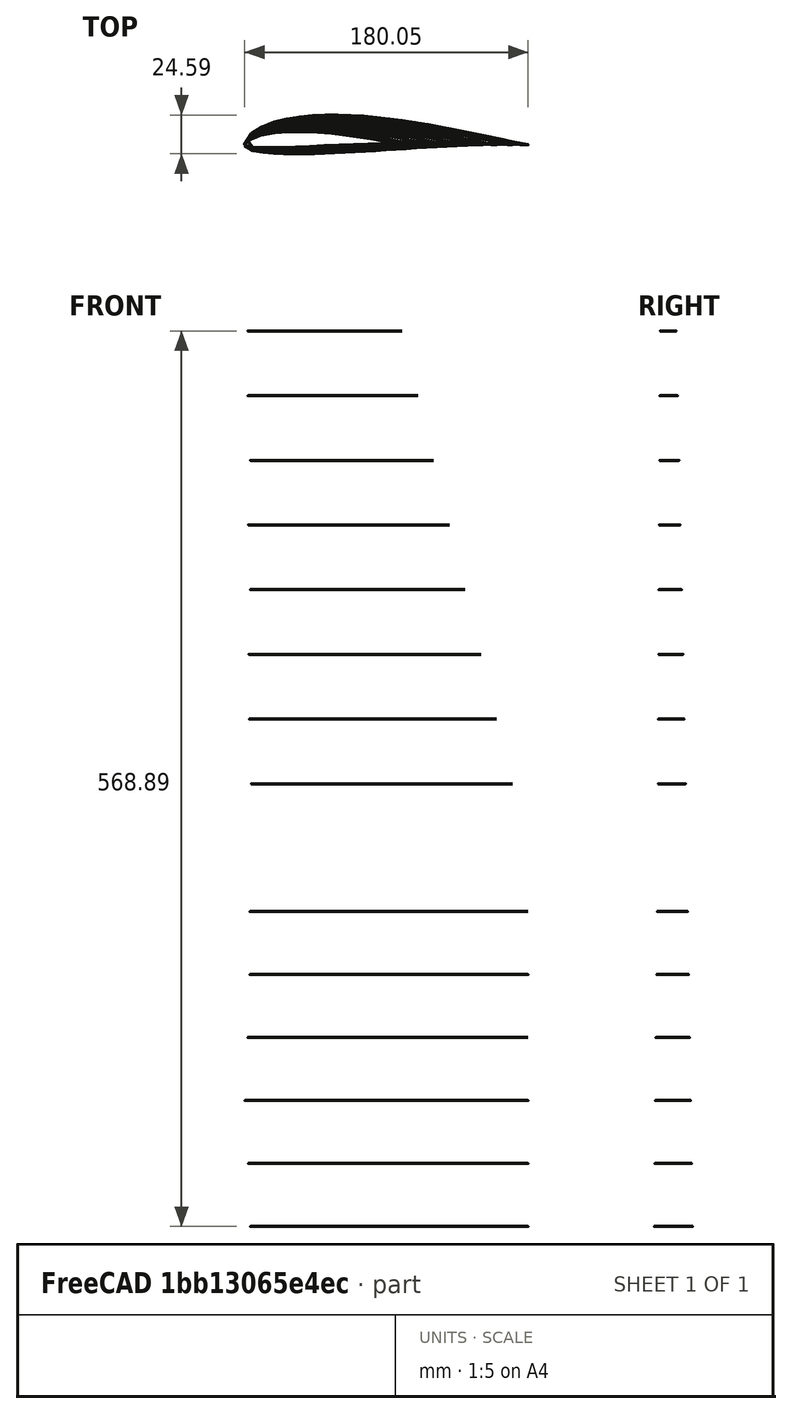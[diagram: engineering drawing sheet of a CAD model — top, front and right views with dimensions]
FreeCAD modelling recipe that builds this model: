
FCSTD DOCUMENT  (FreeCAD 0.21R33771 (Git))
Label: SD7034_wng9
License: All rights reserved
LicenseURL: http://en.wikipedia.org/wiki/All_rights_reserved
objects: Part::Part2DObjectPython×23, Part::MultiCommon×14, App::MeasureDistance×6, App::DocumentObjectGroup×2, Part::Loft×2
note: 39 computed .brp shape members not serialized (recipe doc carries the construction recipe); baked Part::Feature solids carry a one-line shape summary decoded from their .brp

FEATURE [App::DocumentObjectGroup] profile_sd7062_il  label="profile_sd7062-il"
FEATURE [Part::Part2DObjectPython] Wire  # Draft 2D object (typed FeaturePython)
  ChamferSize = 0
  Closed = true
  End = (1,0,0)
  FilletRadius = 0
  Length = 2.05949
  MakeFace = true
  Points = (61) [(1,0,0),(0.99652,0.00057,0),(0.98634,0.00242,0),(0.97004,0.00571,0),(0.94818,0.01036,0),(0.92127,0.01615,0),(0.88967,0.02289,0),(0.85381,0.03049,0),+53 more]
  Start = (1,0,0)
  Subdivisions = 0
FEATURE [Part::Part2DObjectPython] BSpline  # Draft 2D object (typed FeaturePython)
  Closed = true
  MakeFace = true
  Parameterization = 1
  Points = (60) [(1,0,0),(0.99652,0.00057,0),(0.98634,0.00242,0),(0.97004,0.00571,0),(0.94818,0.01036,0),(0.92127,0.01615,0),(0.88967,0.02289,0),(0.85381,0.03049,0),+52 more]
FEATURE [App::DocumentObjectGroup] profile_SD7032_099_88  label="profile_SD7032-099-88"
FEATURE [Part::Part2DObjectPython] Wire001  # Draft 2D object (typed FeaturePython)
  ChamferSize = 0
  Closed = true
  End = (1,0,0)
  FilletRadius = 0
  Length = 2.03505
  MakeFace = true
  Points = (61) [(1,0,0),(0.99674,0.00048,0),(0.98712,0.00204,0),(0.97155,0.00485,0),(0.95054,0.00894,0),(0.92464,0.0142,0),(0.89436,0.02041,0),(0.86021,0.02731,0),+53 more]
  Start = (1,0,0)
  Subdivisions = 0
FEATURE [Part::Part2DObjectPython] BSpline001  # Draft 2D object (typed FeaturePython)
  Closed = true
  MakeFace = true
  Parameterization = 1
  Points = (60) [(1,0,0),(0.99674,0.00048,0),(0.98712,0.00204,0),(0.97155,0.00485,0),(0.95054,0.00894,0),(0.92464,0.0142,0),(0.89436,0.02041,0),(0.86021,0.02731,0),+52 more]
FEATURE [Part::Part2DObjectPython] Clone2D  label="BSpline (2D)"  # Draft 2D object (typed FeaturePython)
  Fuse = false
  Objects = -> [BSpline]
  Scale = (180,180,1)
FEATURE [Part::Part2DObjectPython] Clone2D001  label="BSpline001 (2D)"  # Draft 2D object (typed FeaturePython)
  Fuse = false
  Objects = -> [BSpline001]
  Placement = pos=(0,0,280) rot=(0,0,1;0rad)
  Scale = (180,180,1)
FEATURE [Part::Loft] Loft
  Closed = false
  MaxDegree = 5
  Ruled = false
  Sections = -> [Clone2D,Clone2D001]
  Solid = true
FEATURE [Part::Part2DObjectPython] Clone2D002  label="BSpline001 (2D)001"  # Draft 2D object (typed FeaturePython)
  Fuse = false
  Objects = -> [BSpline001]
  Placement = pos=(0,0,280) rot=(0,0,1;0rad)
  Scale = (180,180,1)
FEATURE [Part::Part2DObjectPython] Clone2D003  label="BSpline001 (2D)002"  # Draft 2D object (typed FeaturePython)
  Fuse = false
  Objects = -> [BSpline001]
  Placement = pos=(0,0,650) rot=(0,0,1;0rad)
  Scale = (90,90,1)
FEATURE [Part::Loft] Loft001
  Closed = false
  MaxDegree = 5
  Ruled = false
  Sections = -> [Clone2D002,Clone2D003]
  Solid = true
FEATURE [Part::Part2DObjectPython] Rectangle  # Draft 2D object (typed FeaturePython)
  ChamferSize = 0
  Columns = 1
  FilletRadius = 0
  Height = 60
  Length = 220
  MakeFace = true
  Placement = pos=(-10,-15,0) rot=(0,0,1;0rad)
  Rows = 1
FEATURE [Part::Part2DObjectPython] Clone2D004  label="Rectangle (2D)"  # Draft 2D object (typed FeaturePython)
  Fuse = false
  Objects = -> [Rectangle]
  Placement = pos=(-15,-20,40) rot=(0,0,1;0rad)
  Scale = (1,1,1)
FEATURE [Part::MultiCommon] Common
  Shapes = -> [Clone2D004,Loft]
FEATURE [Part::Part2DObjectPython] Clone2D005  label="Rectangle (2D)001"  # Draft 2D object (typed FeaturePython)
  Fuse = false
  Objects = -> [Rectangle]
  Placement = pos=(-15,-20,80) rot=(0,0,1;0rad)
  Scale = (1,1,1)
FEATURE [Part::MultiCommon] Common001
  Shapes = -> [Clone2D005,Loft]
FEATURE [Part::Part2DObjectPython] Clone2D006  label="Rectangle (2D)002"  # Draft 2D object (typed FeaturePython)
  Fuse = false
  Objects = -> [Rectangle]
  Placement = pos=(-15,-20,120) rot=(0,0,1;0rad)
  Scale = (1,1,1)
FEATURE [Part::MultiCommon] Common002
  Shapes = -> [Clone2D006,Loft]
FEATURE [Part::Part2DObjectPython] Clone2D007  label="Rectangle (2D)003"  # Draft 2D object (typed FeaturePython)
  Fuse = false
  Objects = -> [Rectangle]
  Placement = pos=(-15,-20,160) rot=(0,0,1;0rad)
  Scale = (1,1,1)
FEATURE [Part::MultiCommon] Common003
  Shapes = -> [Clone2D007,Loft]
FEATURE [Part::Part2DObjectPython] Clone2D008  label="Rectangle (2D)004"  # Draft 2D object (typed FeaturePython)
  Fuse = false
  Objects = -> [Rectangle]
  Placement = pos=(-15,-20,200) rot=(0,0,1;0rad)
  Scale = (1,1,1)
FEATURE [Part::MultiCommon] Common004
  Shapes = -> [Clone2D008,Loft]
FEATURE [Part::Part2DObjectPython] Clone2D009  label="Rectangle (2D)005"  # Draft 2D object (typed FeaturePython)
  Fuse = false
  Objects = -> [Rectangle]
  Placement = pos=(-15,-20,240) rot=(0,0,1;0rad)
  Scale = (1,1,1)
FEATURE [Part::MultiCommon] Common005
  Shapes = -> [Clone2D009,Loft]
FEATURE [Part::Part2DObjectPython] Clone2D010  label="Rectangle (2D)006"  # Draft 2D object (typed FeaturePython)
  Fuse = false
  Objects = -> [Rectangle]
  Placement = pos=(-15,-20,321.111) rot=(0,0,1;0rad)
  Scale = (1,1,1)
FEATURE [Part::MultiCommon] Common006
  Shapes = -> [Clone2D010,Loft001]
FEATURE [Part::Part2DObjectPython] Clone2D011  label="Rectangle (2D)007"  # Draft 2D object (typed FeaturePython)
  Fuse = false
  Objects = -> [Rectangle]
  Placement = pos=(-15,-20,362.222) rot=(0,0,1;0rad)
  Scale = (1,1,1)
FEATURE [Part::MultiCommon] Common007
  Shapes = -> [Clone2D011,Loft001]
FEATURE [Part::Part2DObjectPython] Clone2D012  label="Rectangle (2D)008"  # Draft 2D object (typed FeaturePython)
  Fuse = false
  Objects = -> [Rectangle]
  Placement = pos=(-15,-20,403.333) rot=(0,0,1;0rad)
  Scale = (1,1,1)
FEATURE [Part::MultiCommon] Common008
  Shapes = -> [Clone2D012,Loft001]
FEATURE [Part::Part2DObjectPython] Clone2D013  label="Rectangle (2D)009"  # Draft 2D object (typed FeaturePython)
  Fuse = false
  Objects = -> [Rectangle]
  Placement = pos=(-15,-20,444.444) rot=(0,0,1;0rad)
  Scale = (1,1,1)
FEATURE [Part::MultiCommon] Common009
  Shapes = -> [Clone2D013,Loft001]
FEATURE [Part::Part2DObjectPython] Clone2D014  label="Rectangle (2D)010"  # Draft 2D object (typed FeaturePython)
  Fuse = false
  Objects = -> [Rectangle]
  Placement = pos=(-15,-20,485.556) rot=(0,0,1;0rad)
  Scale = (1,1,1)
FEATURE [Part::MultiCommon] Common010
  Shapes = -> [Clone2D014,Loft001]
FEATURE [Part::Part2DObjectPython] Clone2D015  label="Rectangle (2D)011"  # Draft 2D object (typed FeaturePython)
  Fuse = false
  Objects = -> [Rectangle]
  Placement = pos=(-15,-20,526.667) rot=(0,0,1;0rad)
  Scale = (1,1,1)
FEATURE [Part::MultiCommon] Common011
  Shapes = -> [Clone2D015,Loft001]
FEATURE [Part::Part2DObjectPython] Clone2D016  label="Rectangle (2D)012"  # Draft 2D object (typed FeaturePython)
  Fuse = false
  Objects = -> [Rectangle]
  Placement = pos=(-15,-20,567.778) rot=(0,0,1;0rad)
  Scale = (1,1,1)
FEATURE [Part::MultiCommon] Common012
  Shapes = -> [Clone2D016,Loft001]
FEATURE [Part::Part2DObjectPython] Clone2D017  label="Rectangle (2D)013"  # Draft 2D object (typed FeaturePython)
  Fuse = false
  Objects = -> [Rectangle]
  Placement = pos=(-15,-20,608.889) rot=(0,0,1;0rad)
  Scale = (1,1,1)
FEATURE [Part::MultiCommon] Common013
  Shapes = -> [Clone2D017,Loft001]
FEATURE [App::MeasureDistance] Distance  label="Distance: 89.39 mm"
  Distance = 89.3861
  P1 = (0.622783,1.2597,650)
  P2 = (90,0,650)
FEATURE [App::MeasureDistance] Distance001  label="Distance: 180.0 mm"
  Distance = 180
  P1 = (0,0,0)
  P2 = (180,0,0)
FEATURE [App::MeasureDistance] Distance002  label="Distance: 26.91 mm"
  Distance = 26.9077
  P1 = (57.0083,-5.44953,0)
  P2 = (46.4234,19.2888,0)
FEATURE [App::MeasureDistance] Distance003  label="Distance: 12.19 mm"
  Distance = 12.1933
  P1 = (26.3808,-1.33728,650)
  P2 = (17.4983,7.01597,650)
FEATURE [App::MeasureDistance] Distance004  label="Distance: 179.58 mm"
  Distance = 180
  P1 = (0,0,280)
  P2 = (180,0,280)
FEATURE [App::MeasureDistance] Distance005  label="Distance: 23.22 mm"
  Distance = 23.2242
  P1 = (60.0788,-2.33292,280)
  P2 = (44.4654,14.8596,280)
